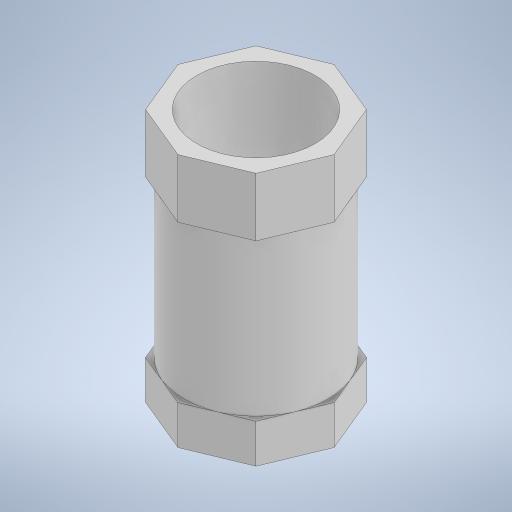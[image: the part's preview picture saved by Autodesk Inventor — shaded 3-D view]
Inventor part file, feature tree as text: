
AUTODESK INVENTOR PART (.ipt)
format: ipt  version: 2024 (Build 280153000, 153)  size: 279,552 bytes
history: native  units: mm
features: other x3, extrude x3, hole x1, sketch x1
ambient origin geometry x8: Origin, YZ Plane, XZ Plane, XY Plane, X Axis, Y Axis, Z Axis, Center Point
bodies: Body1 (feature_tree)
feature tree (8):
  other  "Sólido1"
  extrude  "Extrusión1"  Depth=10.0mm TaperAngle=0.0deg
  extrude  "Extrusión2"  Depth=10.0mm TaperAngle=0.0deg
  extrude  "Extrusión3"  Depth=10.0mm
  hole  "Agujero1"  [1 undecoded]
  other  "Edición directa1"
  sketch  "Boceto1"  dims[d0=20.0mm d1=5.0mm d2=0.0mm d3=20.0mm d4=0.0mm d5=20.0mm d6=7.5mm d7=0.0mm d8=15.1638mm d9=32.5mm d10=4.0mm d11=2.0mm d12=90.0deg d13=8.0mm d14=20.594885mm d15=2.666666mm d16=10.0mm d17=10.0mm]
  other  "Escala1"
note: 1 required parameter value undecoded (feature->parameter linkage not recoverable at this tier; creation-order binding heuristic only, values carry confidence <= 0.55)
